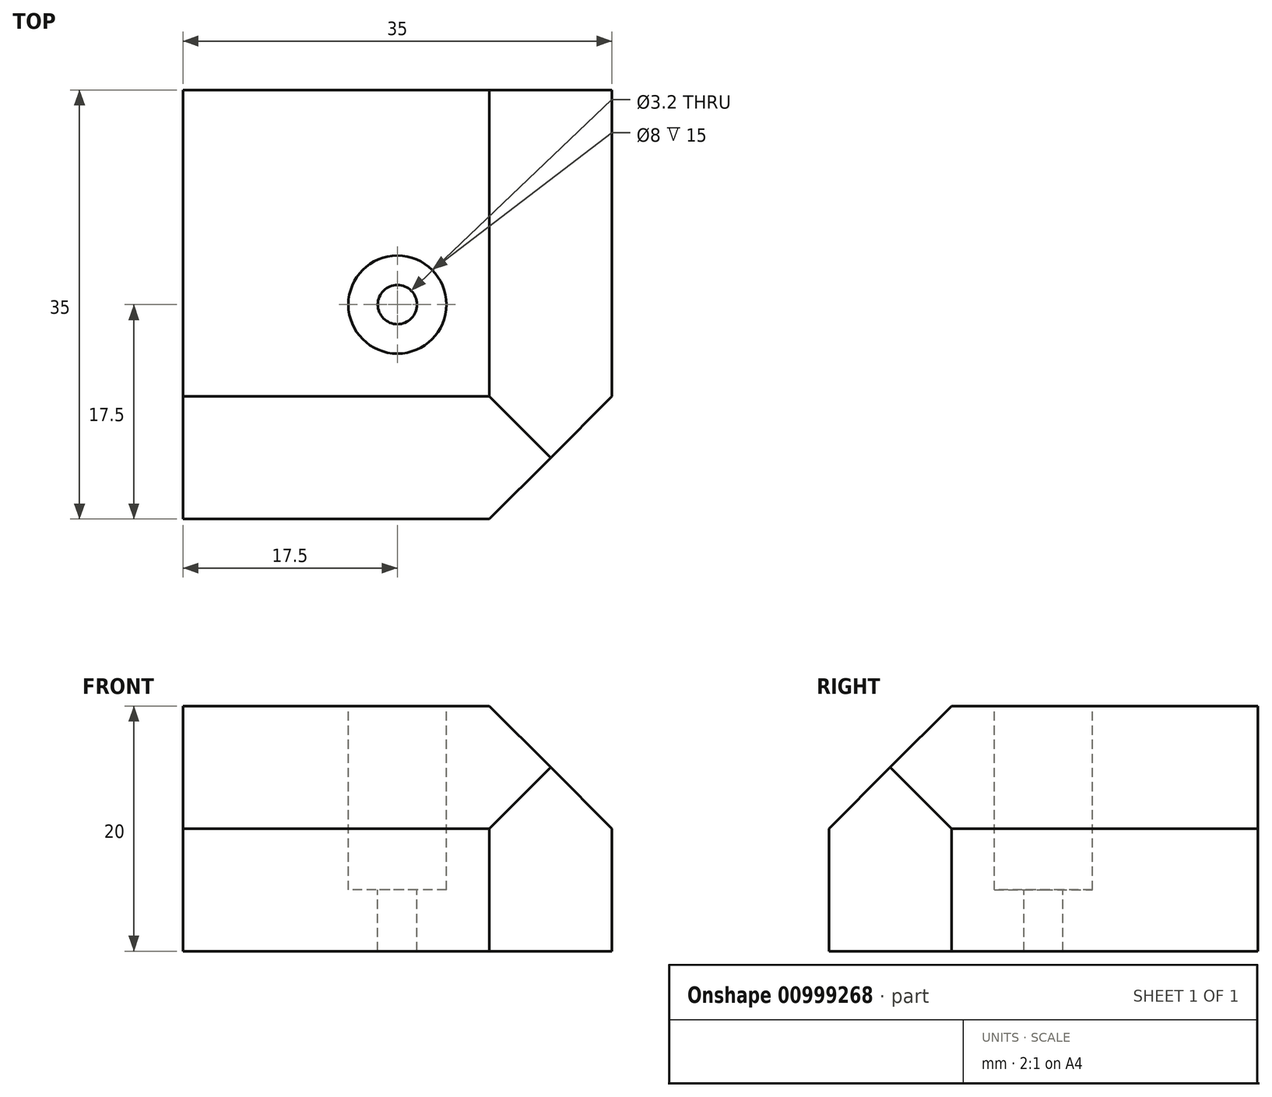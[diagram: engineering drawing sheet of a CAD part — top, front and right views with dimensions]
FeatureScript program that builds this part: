
annotation { "Feature Type Name" : "Feature", "Feature Type Description" : "" }
export const myFeature = defineFeature(function(context is Context, id is Id, definition is map)
    precondition{}
    {
        {
            var Q0;
            Q0=qCreatedBy(makeId("Top.planeOp"),FACE);
            var sketch = newSketch(context, id + "F0", { "sketchPlane" : qUnion([Q0])});
            skLineSegment(sketch, "E0.bottom", {"start": v(0, 0) * mm, "end": v(35, 0) * mm});
            skLineSegment(sketch, "E0.top", {"start": v(0, -35) * mm, "end": v(35, -35) * mm});
            skLineSegment(sketch, "E0.left", {"start": v(0, 0) * mm, "end": v(0, -35) * mm});
            skLineSegment(sketch, "E0.right", {"start": v(35, 0) * mm, "end": v(35, -35) * mm});
            skSolve(sketch);
        }
        {
            var Q0;
            Q0=makeQuery(id+"F0.imprint","IMPRINT",FACE,{"disambiguationData":[TD([[makeQuery(id+"F0.imprint","IMPRINT",EDGE,{"derivedFrom":sQuery(id+"F0.wireOp",EDGE,"E0.bottom")}),-1.0]])]});
            var Q1;
            Q1 = qBodyType(qCreatedBy(id + "F2" ,EDGE), BodyType.WIRE);
            cPlane(context, id + "F1", {"entities" : qUnion([Q0, Q1]), "cplaneType" : CPlaneType.OFFSET, "offset" : 10 * mm, "width" : 150 * mm, "height" : 150 * mm});
        }
        {
            var Q0;
            Q0=qCreatedBy(id+"F1.planeOp",FACE);
            var sketch = newSketch(context, id + "F2", { "sketchPlane" : qUnion([Q0])});
            skLineSegment(sketch, "E1.bottom", {"start": v(0, 0) * mm, "end": v(25, 0) * mm});
            skLineSegment(sketch, "E1.top", {"start": v(0, -25) * mm, "end": v(25, -25) * mm});
            skLineSegment(sketch, "E1.left", {"start": v(0, 0) * mm, "end": v(0, -25) * mm});
            skLineSegment(sketch, "E1.right", {"start": v(25, 0) * mm, "end": v(25, -25) * mm});
            skSolve(sketch);
        }
        {
            var Q0;
            Q0=makeQuery(id+"F0.imprint","IMPRINT",FACE,{"disambiguationData":[TD([[makeQuery(id+"F0.imprint","IMPRINT",EDGE,{"derivedFrom":sQuery(id+"F0.wireOp",EDGE,"E0.bottom")}),-1.0]])]});
            var Q1;
            Q1 = qSketchRegion(id + "F2", true);
            loft(context, id + "F3", {"sheetProfilesArray" : [{ "sheetProfileEntities" : qUnion([Q0]) }, { "sheetProfileEntities" : qUnion([Q1]) }]});
        }
        {
            var Q0;
            Q0=makeQuery(id+"F3.opLoft","CAP_FACE",FACE,{"disambiguationData":[OSD([makeQuery(id+"F0.imprint","IMPRINT",FACE,{"disambiguationData":[TD([[makeQuery(id+"F0.imprint","IMPRINT",EDGE,{"derivedFrom":sQuery(id+"F0.wireOp",EDGE,"E0.bottom")}),-1.0]])]})])],"isStart":true});
            var sketch = newSketch(context, id + "F4", { "sketchPlane" : qUnion([Q0])});
            skLineSegment(sketch, "E2", {"start": v(0, 0) * mm, "end": v(35, 35) * mm, "construction": true});
            skCircle(sketch, "E3", {"center": v(17.5, 17.5) * mm, "radius": 1.6 * mm});
            skSolve(sketch);
        }
        {
            var Q0;
            Q0=makeQuery(id+"F4.imprint","IMPRINT",FACE,{"disambiguationData":[TD([[makeQuery(id+"F4.imprint","IMPRINT",EDGE,{"derivedFrom":sQuery(id+"F4.wireOp",EDGE,"E3")}),-1.0]])]});
            extrude(context, id + "F5", {"entities" : qUnion([Q0]), "operationType" : NewBodyOperationType.ADD, "depth" : 10 * mm, "offsetDistance" : 25 * mm});
        }
        {
            var Q0;
            Q0 = qSketchRegion(id + "F4", true);
            extrude(context, id + "F6", {"entities" : qUnion([Q0]), "operationType" : NewBodyOperationType.REMOVE, "endBound" : BoundingType.THROUGH_ALL, "oppositeDirection" : true, "depth" : 61.37 * mm, "offsetDistance" : 25 * mm});
        }
        {
            var Q0;
            Q0=makeQuery(id+"F3.opLoft","CAP_FACE",FACE,{"disambiguationData":[OSD([makeQuery(id+"F2.imprint","IMPRINT",FACE,{"disambiguationData":[TD([[makeQuery(id+"F2.imprint","IMPRINT",EDGE,{"derivedFrom":sQuery(id+"F2.wireOp",EDGE,"E1.bottom")}),-1.0]])]})])],"isStart":true});
            var sketch = newSketch(context, id + "F7", { "sketchPlane" : qUnion([Q0])});
            skCircle(sketch, "E4", {"center": v(17.5, -17.5) * mm, "radius": 4 * mm});
            skSolve(sketch);
        }
        {
            var Q0;
            Q0=makeQuery(id+"F7.imprint","IMPRINT",FACE,{"disambiguationData":[TD([[makeQuery(id+"F7.imprint","IMPRINT",EDGE,{"derivedFrom":sQuery(id+"F7.wireOp",EDGE,"E4")}),1.0]])]});
            extrude(context, id + "F8", {"entities" : qUnion([Q0]), "operationType" : NewBodyOperationType.REMOVE, "oppositeDirection" : true, "depth" : 15 * mm, "offsetDistance" : 25 * mm});
        }
        {
            var Q0;
            Q0=makeQuery(id+"F5.opExtrude","CAP_FACE",FACE,{"disambiguationData":[OSD([sQuery(id+"F0.wireOp",EDGE,"E0.bottom"),sQuery(id+"F0.wireOp",EDGE,"E0.top"),sQuery(id+"F0.wireOp",EDGE,"E0.left"),sQuery(id+"F0.wireOp",EDGE,"E0.right"),sQuery(id+"F4.wireOp",EDGE,"E3")])],"isStart":false});
            var sketch = newSketch(context, id + "F9", { "sketchPlane" : qUnion([Q0])});
            skLineSegment(sketch, "E5.bottom", {"start": v(35, 35) * mm, "end": v(25, 35) * mm});
            skLineSegment(sketch, "E5.top", {"start": v(35, 25) * mm, "end": v(25, 25) * mm});
            skLineSegment(sketch, "E5.left", {"start": v(35, 35) * mm, "end": v(35, 25) * mm});
            skLineSegment(sketch, "E5.right", {"start": v(25, 35) * mm, "end": v(25, 25) * mm});
            skLineSegment(sketch, "E6", {"start": v(25, 35) * mm, "end": v(35, 25) * mm});
            skSolve(sketch);
        }
        {
            var Q0;
            Q0=makeQuery(id+"F9.imprint","IMPRINT",FACE,{"disambiguationData":[TD([[makeQuery(id+"F9.imprint","IMPRINT",EDGE,{"derivedFrom":sQuery(id+"F9.wireOp",EDGE,"E5.bottom")}),-1.0]])]});
            extrude(context, id + "F10", {"entities" : qUnion([Q0]), "operationType" : NewBodyOperationType.REMOVE, "oppositeDirection" : true, "depth" : 25 * mm, "offsetDistance" : 25 * mm});
        }
    });
